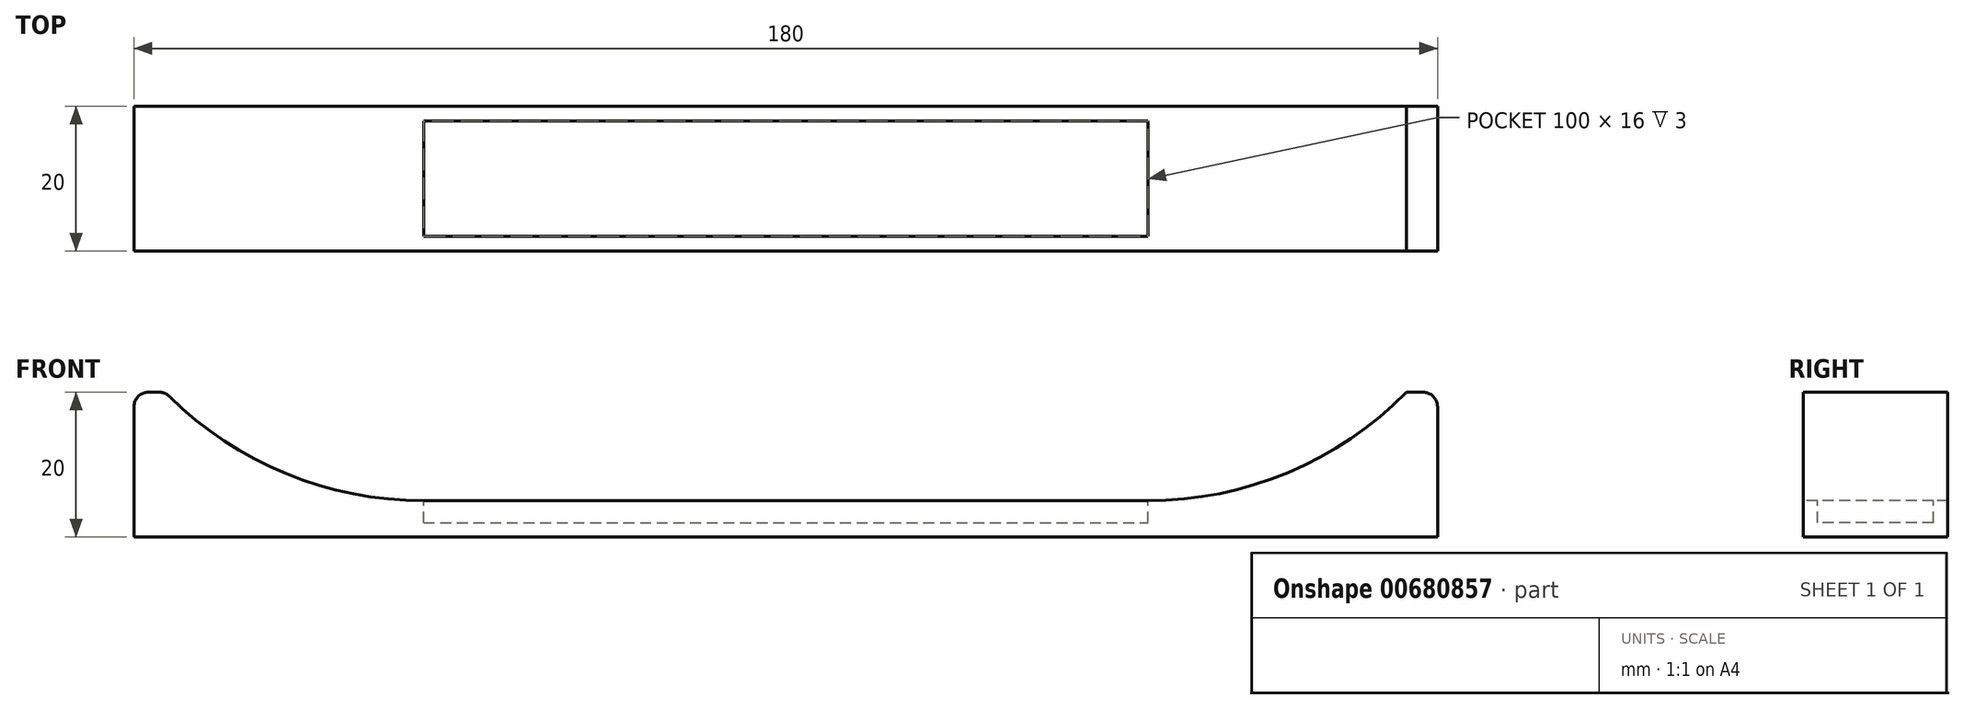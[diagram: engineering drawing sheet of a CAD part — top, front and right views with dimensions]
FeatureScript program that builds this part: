
annotation { "Feature Type Name" : "Feature", "Feature Type Description" : "" }
export const myFeature = defineFeature(function(context is Context, id is Id, definition is map)
    precondition{}
    {
        {
            var Q0;
            Q0=qCreatedBy(makeId("Front.planeOp"),FACE);
            var sketch = newSketch(context, id + "F0", { "sketchPlane" : qUnion([Q0])});
            skLineSegment(sketch, "E0.bottom", {"start": v(0, 0) * mm, "end": v(180, 0) * mm});
            skLineSegment(sketch, "E0.top", {"start": v(0, 20) * mm, "end": v(180, 20) * mm});
            skLineSegment(sketch, "E0.left", {"start": v(0, 0) * mm, "end": v(0, 20) * mm});
            skLineSegment(sketch, "E0.right", {"start": v(180, 0) * mm, "end": v(180, 20) * mm});
            skSolve(sketch);
        }
        {
            var Q0;
            Q0=qSketchRegion(id+"F0",true);
            extrude(context, id + "F1", {"entities" : qUnion([Q0]), "oppositeDirection" : true, "depth" : 20 * mm, "offsetDistance" : 25 * mm});
        }
        {
            var Q0;
            Q0=makeQuery(id+"F1.opExtrude","CAP_FACE",FACE,{"disambiguationData":[OSD([sQuery(id+"F0.wireOp",EDGE,"E0.bottom"),sQuery(id+"F0.wireOp",EDGE,"E0.top"),sQuery(id+"F0.wireOp",EDGE,"E0.left"),sQuery(id+"F0.wireOp",EDGE,"E0.right")])],"isStart":true});
            var sketch = newSketch(context, id + "F2", { "sketchPlane" : qUnion([Q0])});
            skLineSegment(sketch, "E1", {"start": v(0, 0) * mm, "end": v(40, 0) * mm, "construction": true});
            skLineSegment(sketch, "E2", {"start": v(40, 0) * mm, "end": v(40, 55) * mm, "construction": true});
            skCircle(sketch, "E3", {"center": v(40, 55) * mm, "radius": 50 * mm});
            skLineSegment(sketch, "E4", {"start": v(40, 55) * mm, "end": v(140, 55) * mm, "construction": true});
            skCircle(sketch, "E5", {"center": v(140, 55) * mm, "radius": 50 * mm});
            skLineSegment(sketch, "E6", {"start": v(40, 5) * mm, "end": v(140, 5) * mm});
            skSolve(sketch);
        }
        {
            var Q0;
            {var subQ0=sQuery(id+"F2.wireOp",EDGE,"E3");var subQ1=makeQuery(id+"F1.opExtrude","CAP_EDGE",EDGE,{"disambiguationData":[OSD([sQuery(id+"F0.wireOp",EDGE,"E0.top")])],"isStart":true});var subQ2=makeQuery(id+"F2.imprint","INTERSECT",VERTEX,{"disambiguationData":[OD(0.0)],"derivedFrom":[subQ1,subQ0]});Q0=makeQuery(id+"F2.imprint","IMPRINT",FACE,{"disambiguationData":[TD([[makeQuery(id+"F2.imprint","IMPRINT",EDGE,{"disambiguationData":[TD([[subQ2,-1.0]])],"derivedFrom":subQ0}),1.0]])]});}
            var Q1;
            {var subQ0=sQuery(id+"F2.wireOp",EDGE,"E5");var subQ1=makeQuery(id+"F1.opExtrude","CAP_EDGE",EDGE,{"disambiguationData":[OSD([sQuery(id+"F0.wireOp",EDGE,"E0.top")])],"isStart":true});var subQ2=makeQuery(id+"F2.imprint","INTERSECT",VERTEX,{"disambiguationData":[OD(0.0)],"derivedFrom":[subQ1,subQ0]});Q1=makeQuery(id+"F2.imprint","IMPRINT",FACE,{"disambiguationData":[TD([[makeQuery(id+"F2.imprint","IMPRINT",EDGE,{"disambiguationData":[TD([[subQ2,1.0]])],"derivedFrom":subQ0}),1.0]])]});}
            var Q2;
            {var subQ0=sQuery(id+"F2.wireOp",EDGE,"E6");Q2=makeQuery(id+"F2.imprint","IMPRINT",FACE,{"disambiguationData":[TD([[makeQuery(id+"F2.imprint","IMPRINT",EDGE,{"derivedFrom":subQ0}),1.0]])]});}
            extrude(context, id + "F3", {"entities" : qUnion([Q0, Q1, Q2]), "operationType" : NewBodyOperationType.REMOVE, "oppositeDirection" : true, "depth" : 25 * mm, "offsetDistance" : 25 * mm});
        }
        {
            var Q0;
            Q0=makeQuery(id+"F1.opExtrude","SWEPT_EDGE",EDGE,{"disambiguationData":[OSD([sQuery(id+"F0.wireOp",EDGE,"E0.top"),sQuery(id+"F0.wireOp",EDGE,"E0.left")])]});
            var Q1;
            {var subQ0=sQuery(id+"F2.wireOp",EDGE,"E3");var subQ1=sQuery(id+"F0.wireOp",EDGE,"E0.top");Q1=makeQuery(id+"F3.boolean.opBoolean","COPY",EDGE,{"derivedFrom":makeQuery(id+"F3.opExtrude","SWEPT_EDGE",EDGE,{"disambiguationData":[OSD([subQ1,subQ0]),TDD([makeQuery(id+"F2.imprint","INTERSECT",VERTEX,{"disambiguationData":[OD(0.0)],"derivedFrom":[makeQuery(id+"F1.opExtrude","CAP_EDGE",EDGE,{"disambiguationData":[OSD([subQ1])],"isStart":true}),subQ0]})])]})});}
            var Q2;
            {var subQ0=sQuery(id+"F2.wireOp",EDGE,"E3");var subQ1=sQuery(id+"F0.wireOp",EDGE,"E0.top");Q2=makeQuery(id+"F3.boolean.opBoolean","COPY",EDGE,{"derivedFrom":makeQuery(id+"F3.opExtrude","SWEPT_EDGE",EDGE,{"disambiguationData":[OSD([subQ1,subQ0]),TDD([makeQuery(id+"F2.imprint","INTERSECT",VERTEX,{"disambiguationData":[OD(1.0)],"derivedFrom":[makeQuery(id+"F1.opExtrude","CAP_EDGE",EDGE,{"disambiguationData":[OSD([subQ1])],"isStart":true}),subQ0]})])]})});}
            var Q3;
            {var subQ0=sQuery(id+"F2.wireOp",EDGE,"E5");var subQ1=sQuery(id+"F0.wireOp",EDGE,"E0.top");Q3=makeQuery(id+"F3.boolean.opBoolean","COPY",EDGE,{"derivedFrom":makeQuery(id+"F3.opExtrude","SWEPT_EDGE",EDGE,{"disambiguationData":[OSD([subQ1,subQ0]),TDD([makeQuery(id+"F2.imprint","INTERSECT",VERTEX,{"disambiguationData":[OD(1.0)],"derivedFrom":[makeQuery(id+"F1.opExtrude","CAP_EDGE",EDGE,{"disambiguationData":[OSD([subQ1])],"isStart":true}),subQ0]})])]})});}
            var Q4;
            {var subQ0=sQuery(id+"F2.wireOp",EDGE,"E5");var subQ1=sQuery(id+"F0.wireOp",EDGE,"E0.top");Q4=makeQuery(id+"F3.boolean.opBoolean","COPY",EDGE,{"derivedFrom":makeQuery(id+"F3.opExtrude","SWEPT_EDGE",EDGE,{"disambiguationData":[OSD([subQ1,subQ0]),TDD([makeQuery(id+"F2.imprint","INTERSECT",VERTEX,{"disambiguationData":[OD(0.0)],"derivedFrom":[makeQuery(id+"F1.opExtrude","CAP_EDGE",EDGE,{"disambiguationData":[OSD([subQ1])],"isStart":true}),subQ0]})])]})});}
            var Q5;
            Q5=makeQuery(id+"F1.opExtrude","SWEPT_EDGE",EDGE,{"disambiguationData":[OSD([sQuery(id+"F0.wireOp",EDGE,"E0.top"),sQuery(id+"F0.wireOp",EDGE,"E0.right")])]});
            fillet(context, id + "F4", {"entities" : qUnion([Q0, Q1, Q2, Q3, Q4, Q5]), "radius" : 2 * mm, "tangentPropagation" : true, "allowEdgeOverflow" : false});
        }
        {
            var Q0;
            Q0=makeQuery(id+"F3.boolean.opBoolean","COPY",FACE,{"derivedFrom":makeQuery(id+"F3.opExtrude","SWEPT_FACE",FACE,{"disambiguationData":[OSD([sQuery(id+"F2.wireOp",EDGE,"E6")])]})});
            var sketch = newSketch(context, id + "F5", { "sketchPlane" : qUnion([Q0])});
            skLineSegment(sketch, "E7", {"start": v(40, 0) * mm, "end": v(40, 2) * mm});
            skLineSegment(sketch, "E8", {"start": v(40, 2) * mm, "end": v(140, 2) * mm});
            skLineSegment(sketch, "E9", {"start": v(140, 2) * mm, "end": v(140, 18) * mm});
            skLineSegment(sketch, "E10", {"start": v(140, 18) * mm, "end": v(40, 18) * mm});
            skLineSegment(sketch, "E11", {"start": v(40, 18) * mm, "end": v(40, 2) * mm});
            skSolve(sketch);
        }
        {
            var Q0;
            Q0=makeQuery(id+"F5.imprint","IMPRINT",FACE,{"disambiguationData":[TD([[makeQuery(id+"F5.imprint","IMPRINT",EDGE,{"derivedFrom":sQuery(id+"F5.wireOp",EDGE,"E8")}),1.0]])]});
            extrude(context, id + "F6", {"entities" : qUnion([Q0]), "operationType" : NewBodyOperationType.REMOVE, "oppositeDirection" : true, "depth" : 3 * mm, "offsetDistance" : 25 * mm});
        }
    });
